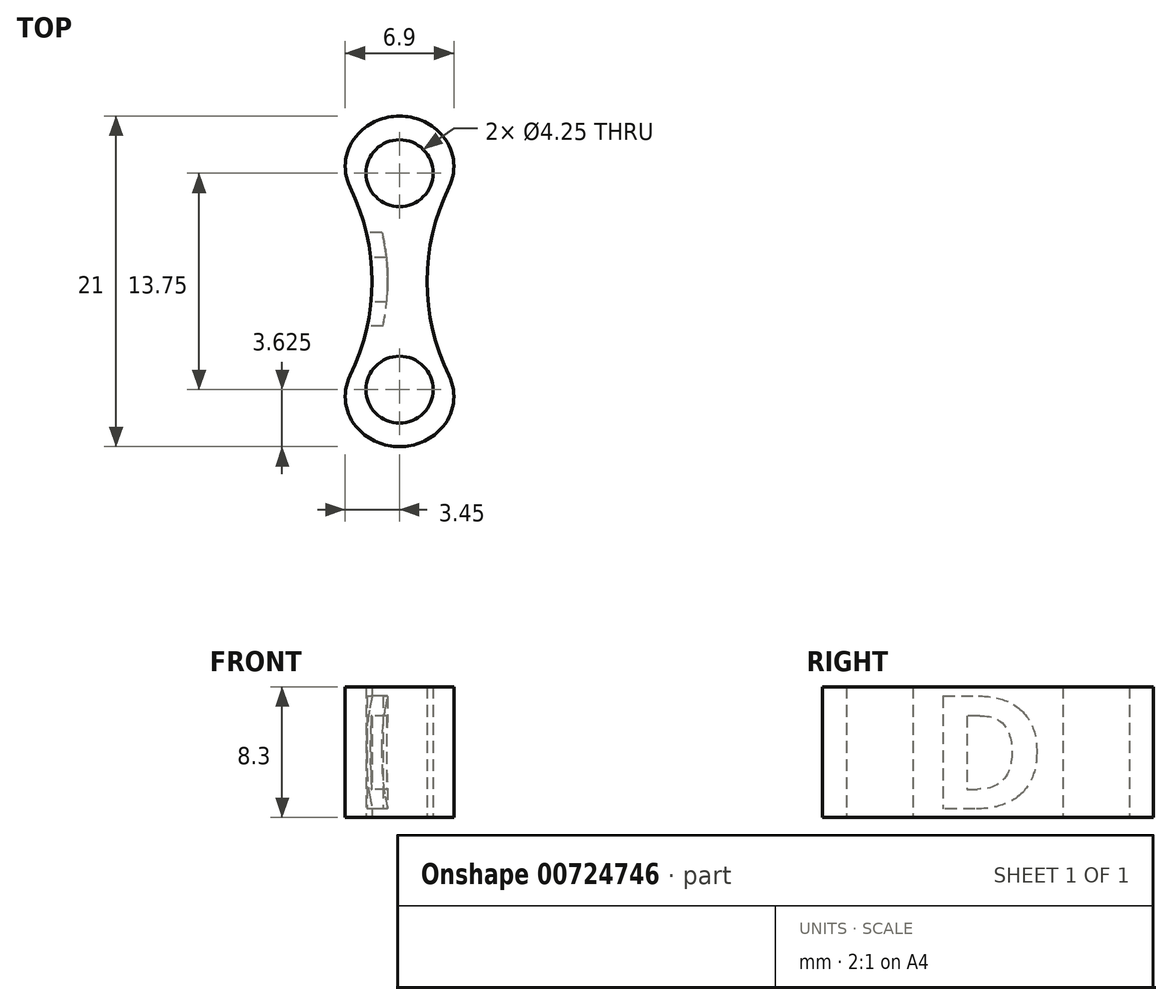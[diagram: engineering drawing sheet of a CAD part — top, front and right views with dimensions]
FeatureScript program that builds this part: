
annotation { "Feature Type Name" : "Feature", "Feature Type Description" : "" }
export const myFeature = defineFeature(function(context is Context, id is Id, definition is map)
    precondition{}
    {
        {
            var Q0;
            Q0=qCreatedBy(makeId("Top.planeOp"),FACE);
            var sketch = newSketch(context, id + "F0", { "sketchPlane" : qUnion([Q0])});
            skLineSegment(sketch, "E0", {"start": v(0, 6.88) * mm, "end": v(0, -6.88) * mm});
            skCircle(sketch, "E1", {"center": v(0, 6.88) * mm, "radius": 2.12 * mm});
            skLineSegment(sketch, "E2", {"start": v(-1.75, 0) * mm, "end": v(1.75, 0) * mm});
            skCircle(sketch, "E3", {"center": v(0, -6.88) * mm, "radius": 2.12 * mm});
            skCircle(sketch, "E4", {"center": v(0, 6.88) * mm, "radius": 3.62 * mm});
            skCircle(sketch, "E5", {"center": v(0, -6.88) * mm, "radius": 3.62 * mm});
            skArc(sketch, "E6", {"start": v(-3.12, -5.03) * mm, "mid": v(-1.75, 0) * mm, "end": v(-3.12, 5.03) * mm});
            skArc(sketch, "E7.MirrorCS", {"start": v(3.12, -5.03) * mm, "mid": v(1.75, 0) * mm, "end": v(3.12, 5.03) * mm});
            skPoint(sketch, "E8.orphan", {"position": v(3.12, 5.03) * mm});
            skPoint(sketch, "E9.orphan", {"position": v(-3.12, 5.03) * mm});
            skPoint(sketch, "E10.orphan", {"position": v(6.24, 6.88) * mm});
            skArc(sketch, "E11", {"start": v(-3.63, -6.87) * mm, "mid": v(-1.75, 0) * mm, "end": v(-3.63, 6.87) * mm});
            skArc(sketch, "E12.MirrorCS", {"start": v(3.63, -6.87) * mm, "mid": v(1.75, 0) * mm, "end": v(3.63, 6.87) * mm});
            skSolve(sketch);
        }
        {
            var Q0;
            Q0=makeQuery(id+"F0.imprint","IMPRINT",FACE,{"disambiguationData":[TD([[makeQuery(id+"F0.imprint","IMPRINT",EDGE,{"derivedFrom":sQuery(id+"F0.wireOp",EDGE,"E1")}),-1.0]])]});
            var Q1;
            {var subQ0=sQuery(id+"F0.wireOp",EDGE,"E4");var subQ1=sQuery(id+"F0.wireOp",EDGE,"E0");var subQ2=makeQuery(id+"F0.imprint","INTERSECT",VERTEX,{"derivedFrom":[subQ1,subQ0]});Q1=makeQuery(id+"F0.imprint","IMPRINT",FACE,{"disambiguationData":[TD([[makeQuery(id+"F0.imprint","IMPRINT",EDGE,{"disambiguationData":[TD([[subQ2,-1.0]])],"derivedFrom":subQ1}),-1.0]])]});}
            var Q2;
            {var subQ0=sQuery(id+"F0.wireOp",EDGE,"E4");var subQ1=sQuery(id+"F0.wireOp",EDGE,"E0");var subQ2=makeQuery(id+"F0.imprint","INTERSECT",VERTEX,{"derivedFrom":[subQ1,subQ0]});Q2=makeQuery(id+"F0.imprint","IMPRINT",FACE,{"disambiguationData":[TD([[makeQuery(id+"F0.imprint","IMPRINT",EDGE,{"disambiguationData":[TD([[subQ2,-1.0]])],"derivedFrom":subQ1}),1.0]])]});}
            var Q3;
            {var subQ0=sQuery(id+"F0.wireOp",EDGE,"E5");var subQ1=sQuery(id+"F0.wireOp",EDGE,"E0");var subQ2=makeQuery(id+"F0.imprint","INTERSECT",VERTEX,{"derivedFrom":[subQ1,subQ0]});Q3=makeQuery(id+"F0.imprint","IMPRINT",FACE,{"disambiguationData":[TD([[makeQuery(id+"F0.imprint","IMPRINT",EDGE,{"disambiguationData":[TD([[subQ2,1.0]])],"derivedFrom":subQ1}),1.0]])]});}
            var Q4;
            {var subQ0=sQuery(id+"F0.wireOp",EDGE,"E5");var subQ1=sQuery(id+"F0.wireOp",EDGE,"E0");var subQ2=makeQuery(id+"F0.imprint","INTERSECT",VERTEX,{"derivedFrom":[subQ1,subQ0]});Q4=makeQuery(id+"F0.imprint","IMPRINT",FACE,{"disambiguationData":[TD([[makeQuery(id+"F0.imprint","IMPRINT",EDGE,{"disambiguationData":[TD([[subQ2,1.0]])],"derivedFrom":subQ1}),-1.0]])]});}
            var Q5;
            Q5=makeQuery(id+"F0.imprint","IMPRINT",FACE,{"disambiguationData":[TD([[makeQuery(id+"F0.imprint","IMPRINT",EDGE,{"derivedFrom":sQuery(id+"F0.wireOp",EDGE,"E3")}),-1.0]])]});
            extrude(context, id + "F1", {"entities" : qUnion([Q0, Q1, Q2, Q3, Q4, Q5]), "depth" : 8.3 * mm, "offsetDistance" : 25 * mm});
        }
        {
            var Q0;
            Q0=makeQuery(id+"F1.opExtrude","CAP_VERTEX",VERTEX,{"disambiguationData":[OSD([sQuery(id+"F0.wireOp",EDGE,"E4"),sQuery(id+"F0.wireOp",EDGE,"E11")])],"isStart":false});
            var Q1;
            Q1=makeQuery(id+"F1.opExtrude","CAP_VERTEX",VERTEX,{"disambiguationData":[OSD([sQuery(id+"F0.wireOp",EDGE,"E4"),sQuery(id+"F0.wireOp",EDGE,"E11")])],"isStart":true});
            var Q2;
            Q2=makeQuery(id+"F1.opExtrude","CAP_VERTEX",VERTEX,{"disambiguationData":[OSD([sQuery(id+"F0.wireOp",EDGE,"E5"),sQuery(id+"F0.wireOp",EDGE,"E11")])],"isStart":true});
            cPlane(context, id + "F2", {"entities" : qUnion([Q0, Q1, Q2]), "cplaneType" : CPlaneType.THREE_POINT, "offset" : 10 * mm, "width" : 150 * mm, "height" : 150 * mm});
        }
        {
            var Q0;
            Q0=qCreatedBy(id+"F2.planeOp",FACE);
            var sketch = newSketch(context, id + "F3", { "sketchPlane" : qUnion([Q0])});
            skLineSegment(sketch, "E13", {"start": v(-1.85, 4.15) * mm, "end": v(1.85, 4.15) * mm});
            skPoint(sketch, "E14", {"position": v(0, 4.15) * mm});
            skSolve(sketch);
        }
        {
            var Q0;
            Q0=qCreatedBy(id+"F2.planeOp",FACE);
            var sketch = newSketch(context, id + "F4", { "sketchPlane" : qUnion([Q0])});
            skText(sketch, "E15", { "text": "D", "fontName": "OpenSans-Bold.ttf"});
            const initialGuessF4  = {"E15": [-0.00375, 0.00054, 1, 0, 0.00723]};
            skSetInitialGuess(sketch, initialGuessF4);
            skSolve(sketch);
        }
        {
            var Q0;
            Q0=makeQuery(id+"F4.imprint","IMPRINT",FACE,{"disambiguationData":[TD([[makeQuery(id+"F4.imprint","IMPRINT",EDGE,{"derivedFrom":sQuery(id+"F4.wireOp",EDGE,"E15.sketch_text.stroke-0")}),-1.0]])]});
            var Q1;
            Q1=makeQuery(id+"F1.opExtrude","SWEPT_FACE",FACE,{"disambiguationData":[OSD([sQuery(id+"F0.wireOp",EDGE,"E11")])]});
            extrude(context, id + "F5", {"entities" : qUnion([Q0]), "operationType" : NewBodyOperationType.REMOVE, "endBound" : BoundingType.UP_TO_SURFACE, "depth" : 25 * mm, "endBoundEntityFace" : qUnion([Q1]), "hasOffset" : true, "offsetDistance" : 1 * mm, "offsetOppositeDirection" : true});
        }
        {
            var Q0;
            Q0=makeQuery(id+"F1.opExtrude","SWEPT_EDGE",EDGE,{"disambiguationData":[OSD([sQuery(id+"F0.wireOp",EDGE,"E4"),sQuery(id+"F0.wireOp",EDGE,"E11")])]});
            var Q1;
            Q1=makeQuery(id+"F1.opExtrude","SWEPT_EDGE",EDGE,{"disambiguationData":[OSD([sQuery(id+"F0.wireOp",EDGE,"E5"),sQuery(id+"F0.wireOp",EDGE,"E11")])]});
            var Q2;
            Q2=makeQuery(id+"F1.opExtrude","SWEPT_EDGE",EDGE,{"disambiguationData":[OSD([sQuery(id+"F0.wireOp",EDGE,"E5"),sQuery(id+"F0.wireOp",EDGE,"E12.MirrorCS")])]});
            var Q3;
            Q3=makeQuery(id+"F1.opExtrude","SWEPT_EDGE",EDGE,{"disambiguationData":[OSD([sQuery(id+"F0.wireOp",EDGE,"E4"),sQuery(id+"F0.wireOp",EDGE,"E12.MirrorCS")])]});
            fillet(context, id + "F6", {"entities" : qUnion([Q0, Q1, Q2, Q3]), "radius" : 3 * mm, "tangentPropagation" : true, "allowEdgeOverflow" : false});
        }
    });
